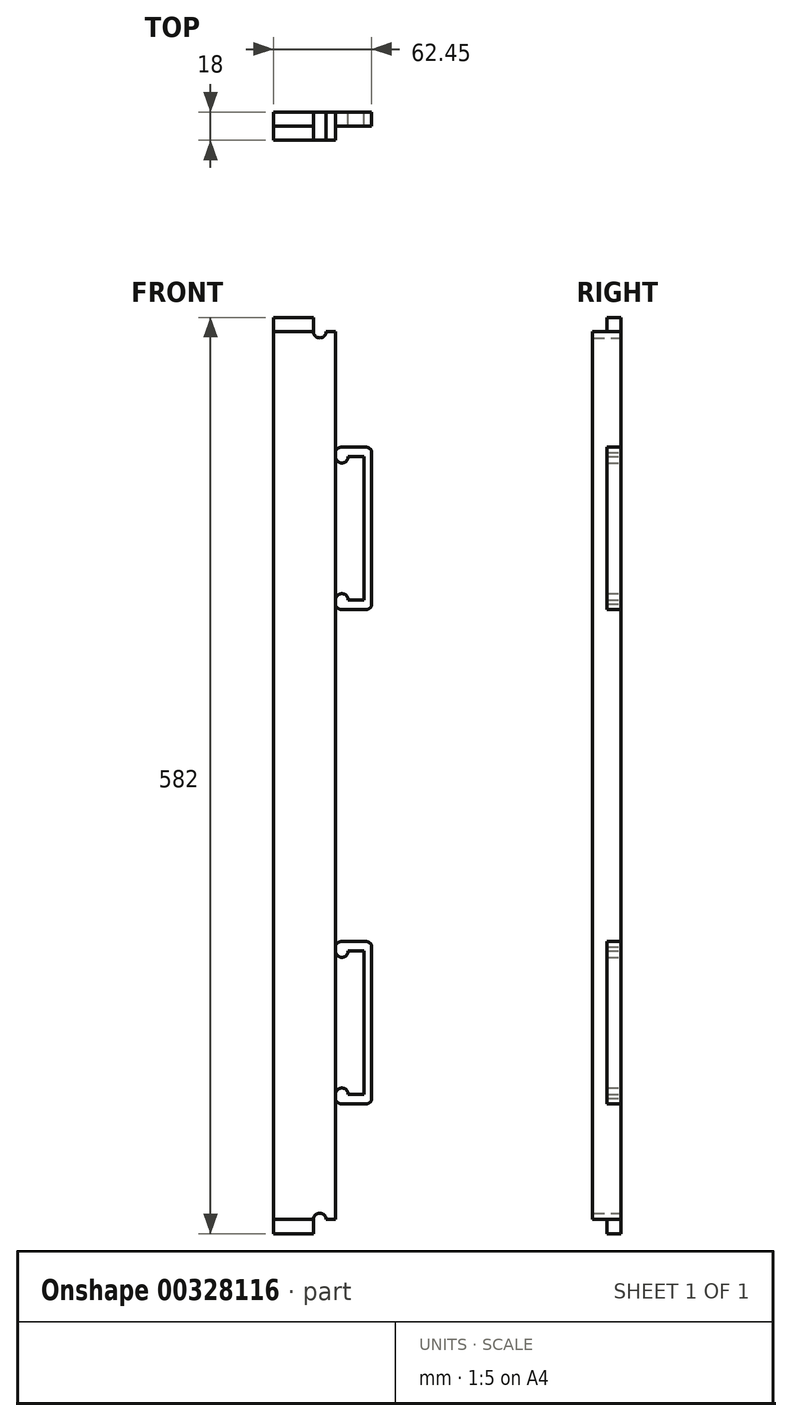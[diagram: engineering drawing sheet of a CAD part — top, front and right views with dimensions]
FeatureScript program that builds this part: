
annotation { "Feature Type Name" : "Feature", "Feature Type Description" : "" }
export const myFeature = defineFeature(function(context is Context, id is Id, definition is map)
    precondition{}
    {
        {
            var Q0;
            Q0=qCreatedBy(makeId("Front.planeOp"),FACE);
            var sketch = newSketch(context, id + "F0", { "sketchPlane" : qUnion([Q0])});
            skLineSegment(sketch, "E0", {"start": v(-27.6, 276.44) * mm, "end": v(-27.6, 355.94) * mm});
            skLineSegment(sketch, "E1", {"start": v(-27.6, 355.94) * mm, "end": v(-33.6, 355.94) * mm});
            skArc(sketch, "E2", {"start": v(-33.6, 355.94) * mm, "mid": v(-37.6, 351.94) * mm, "end": v(-41.6, 355.94) * mm});
            skLineSegment(sketch, "E3", {"start": v(-41.6, 355.94) * mm, "end": v(-41.6, 364.94) * mm});
            skLineSegment(sketch, "E4", {"start": v(-41.6, 364.94) * mm, "end": v(-67.05, 364.94) * mm});
            skLineSegment(sketch, "E5", {"start": v(-67.05, 364.94) * mm, "end": v(-67.05, -217.06) * mm});
            skLineSegment(sketch, "E6", {"start": v(-67.05, -217.06) * mm, "end": v(-41.6, -217.06) * mm});
            skLineSegment(sketch, "E7", {"start": v(-41.6, -217.06) * mm, "end": v(-41.6, -208.06) * mm});
            skArc(sketch, "E8", {"start": v(-41.6, -208.06) * mm, "mid": v(-37.6, -204.06) * mm, "end": v(-33.6, -208.06) * mm});
            skLineSegment(sketch, "E9", {"start": v(-33.6, -208.06) * mm, "end": v(-27.6, -208.06) * mm});
            skLineSegment(sketch, "E10", {"start": v(-27.6, -208.06) * mm, "end": v(-27.6, -128.56) * mm});
            skArc(sketch, "E11", {"start": v(-27.6, -128.56) * mm, "mid": v(-23.6, -124.56) * mm, "end": v(-19.6, -128.56) * mm});
            skLineSegment(sketch, "E12", {"start": v(-19.6, -128.56) * mm, "end": v(-9.6, -128.56) * mm});
            skLineSegment(sketch, "E13", {"start": v(-9.6, -128.56) * mm, "end": v(-9.6, -37.56) * mm});
            skLineSegment(sketch, "E14", {"start": v(-9.6, -37.56) * mm, "end": v(-19.6, -37.56) * mm});
            skArc(sketch, "E15", {"start": v(-19.6, -37.56) * mm, "mid": v(-23.6, -41.56) * mm, "end": v(-27.6, -37.56) * mm});
            skLineSegment(sketch, "E16", {"start": v(-27.6, -37.56) * mm, "end": v(-27.6, 185.44) * mm});
            skArc(sketch, "E17", {"start": v(-27.6, 185.44) * mm, "mid": v(-23.6, 189.44) * mm, "end": v(-19.6, 185.44) * mm});
            skLineSegment(sketch, "E18", {"start": v(-19.6, 185.44) * mm, "end": v(-9.6, 185.44) * mm});
            skLineSegment(sketch, "E19", {"start": v(-9.6, 185.44) * mm, "end": v(-9.6, 276.44) * mm});
            skLineSegment(sketch, "E20", {"start": v(-9.6, 276.44) * mm, "end": v(-19.6, 276.44) * mm});
            skArc(sketch, "E21", {"start": v(-19.6, 276.44) * mm, "mid": v(-23.6, 272.44) * mm, "end": v(-27.6, 276.44) * mm});
            skArc(sketch, "E22", {"start": v(-27.6, 278.94) * mm, "mid": v(-26.57, 281.41) * mm, "end": v(-24.1, 282.44) * mm});
            skLineSegment(sketch, "E23", {"start": v(-24.1, 282.44) * mm, "end": v(-8.1, 282.44) * mm});
            skArc(sketch, "E24", {"start": v(-8.1, 282.44) * mm, "mid": v(-5.62, 281.41) * mm, "end": v(-4.6, 278.94) * mm});
            skLineSegment(sketch, "E25", {"start": v(-4.6, 278.94) * mm, "end": v(-4.6, 182.94) * mm});
            skArc(sketch, "E26", {"start": v(-4.6, 182.94) * mm, "mid": v(-5.62, 180.46) * mm, "end": v(-8.1, 179.44) * mm});
            skLineSegment(sketch, "E27", {"start": v(-8.1, 179.44) * mm, "end": v(-24.1, 179.44) * mm});
            skArc(sketch, "E28", {"start": v(-24.1, 179.44) * mm, "mid": v(-26.57, 180.46) * mm, "end": v(-27.6, 182.94) * mm});
            skLineSegment(sketch, "E29", {"start": v(-27.6, 182.94) * mm, "end": v(-27.6, 278.94) * mm});
            skLineSegment(sketch, "E30", {"start": v(-27.6, -131.06) * mm, "end": v(-27.6, -35.06) * mm});
            skArc(sketch, "E31", {"start": v(-27.6, -35.06) * mm, "mid": v(-26.57, -32.59) * mm, "end": v(-24.1, -31.56) * mm});
            skLineSegment(sketch, "E32", {"start": v(-24.1, -31.56) * mm, "end": v(-8.1, -31.56) * mm});
            skArc(sketch, "E33", {"start": v(-8.1, -31.56) * mm, "mid": v(-5.62, -32.59) * mm, "end": v(-4.6, -35.06) * mm});
            skLineSegment(sketch, "E34", {"start": v(-4.6, -35.06) * mm, "end": v(-4.6, -131.06) * mm});
            skArc(sketch, "E35", {"start": v(-4.6, -131.06) * mm, "mid": v(-5.62, -133.54) * mm, "end": v(-8.1, -134.56) * mm});
            skLineSegment(sketch, "E36", {"start": v(-8.1, -134.56) * mm, "end": v(-24.1, -134.56) * mm});
            skArc(sketch, "E37", {"start": v(-24.1, -134.56) * mm, "mid": v(-26.57, -133.54) * mm, "end": v(-27.6, -131.06) * mm});
            skArc(sketch, "E38", {"start": v(-38.32, -208.06) * mm, "mid": v(-35.85, -209.09) * mm, "end": v(-34.82, -211.56) * mm});
            skLineSegment(sketch, "E39", {"start": v(-34.82, -211.56) * mm, "end": v(-34.82, -227.56) * mm});
            skArc(sketch, "E40", {"start": v(-34.82, -227.56) * mm, "mid": v(-35.85, -230.04) * mm, "end": v(-38.32, -231.06) * mm});
            skLineSegment(sketch, "E41", {"start": v(-38.32, -231.06) * mm, "end": v(-69.1, -231.06) * mm});
            skArc(sketch, "E42", {"start": v(-69.1, -231.06) * mm, "mid": v(-71.57, -230.04) * mm, "end": v(-72.6, -227.56) * mm});
            skLineSegment(sketch, "E43", {"start": v(-72.6, -227.56) * mm, "end": v(-72.6, -211.56) * mm});
            skArc(sketch, "E44", {"start": v(-72.6, -211.56) * mm, "mid": v(-71.57, -209.09) * mm, "end": v(-69.1, -208.06) * mm});
            skLineSegment(sketch, "E45", {"start": v(-69.1, -208.06) * mm, "end": v(-38.32, -208.06) * mm});
            skLineSegment(sketch, "E46", {"start": v(-38.32, 355.94) * mm, "end": v(-69.1, 355.94) * mm});
            skArc(sketch, "E47", {"start": v(-69.1, 355.94) * mm, "mid": v(-71.57, 356.96) * mm, "end": v(-72.6, 359.44) * mm});
            skLineSegment(sketch, "E48", {"start": v(-72.6, 359.44) * mm, "end": v(-72.6, 375.44) * mm});
            skArc(sketch, "E49", {"start": v(-72.6, 375.44) * mm, "mid": v(-71.57, 377.91) * mm, "end": v(-69.1, 378.94) * mm});
            skLineSegment(sketch, "E50", {"start": v(-69.1, 378.94) * mm, "end": v(-38.32, 378.94) * mm});
            skArc(sketch, "E51", {"start": v(-38.32, 378.94) * mm, "mid": v(-35.85, 377.91) * mm, "end": v(-34.82, 375.44) * mm});
            skLineSegment(sketch, "E52", {"start": v(-34.82, 375.44) * mm, "end": v(-34.82, 359.44) * mm});
            skArc(sketch, "E53", {"start": v(-34.82, 359.44) * mm, "mid": v(-35.85, 356.96) * mm, "end": v(-38.32, 355.94) * mm});
            skSolve(sketch);
        }
        {
            var Q0;
            {var subQ9=sQuery(id+"F0.wireOp",EDGE,"E0");Q0=makeQuery(id+"F0.imprint","IMPRINT",FACE,{"disambiguationData":[TD([[makeQuery(id+"F0.imprint","IMPRINT",EDGE,{"derivedFrom":subQ9}),1.0]])]});}
            extrude(context, id + "F1", {"entities" : qUnion([Q0]), "depth" : 18 * mm});
        }
        {
            var Q0;
            {var subQ0=sQuery(id+"F0.wireOp",EDGE,"E3");Q0=makeQuery(id+"F0.imprint","IMPRINT",FACE,{"disambiguationData":[TD([[makeQuery(id+"F0.imprint","IMPRINT",EDGE,{"derivedFrom":subQ0}),1.0]])]});}
            var Q1;
            {var subQ1=sQuery(id+"F0.wireOp",EDGE,"E17");Q1=makeQuery(id+"F0.imprint","IMPRINT",FACE,{"disambiguationData":[TD([[makeQuery(id+"F0.imprint","IMPRINT",EDGE,{"derivedFrom":subQ1}),1.0]])]});}
            var Q2;
            {var subQ0=sQuery(id+"F0.wireOp",EDGE,"E11");Q2=makeQuery(id+"F0.imprint","IMPRINT",FACE,{"disambiguationData":[TD([[makeQuery(id+"F0.imprint","IMPRINT",EDGE,{"derivedFrom":subQ0}),1.0]])]});}
            var Q3;
            {var subQ0=sQuery(id+"F0.wireOp",EDGE,"E6");Q3=makeQuery(id+"F0.imprint","IMPRINT",FACE,{"disambiguationData":[TD([[makeQuery(id+"F0.imprint","IMPRINT",EDGE,{"derivedFrom":subQ0}),1.0]])]});}
            extrude(context, id + "F2", {"entities" : qUnion([Q0, Q1, Q2, Q3]), "operationType" : NewBodyOperationType.ADD, "depth" : 9 * mm});
        }
    });
